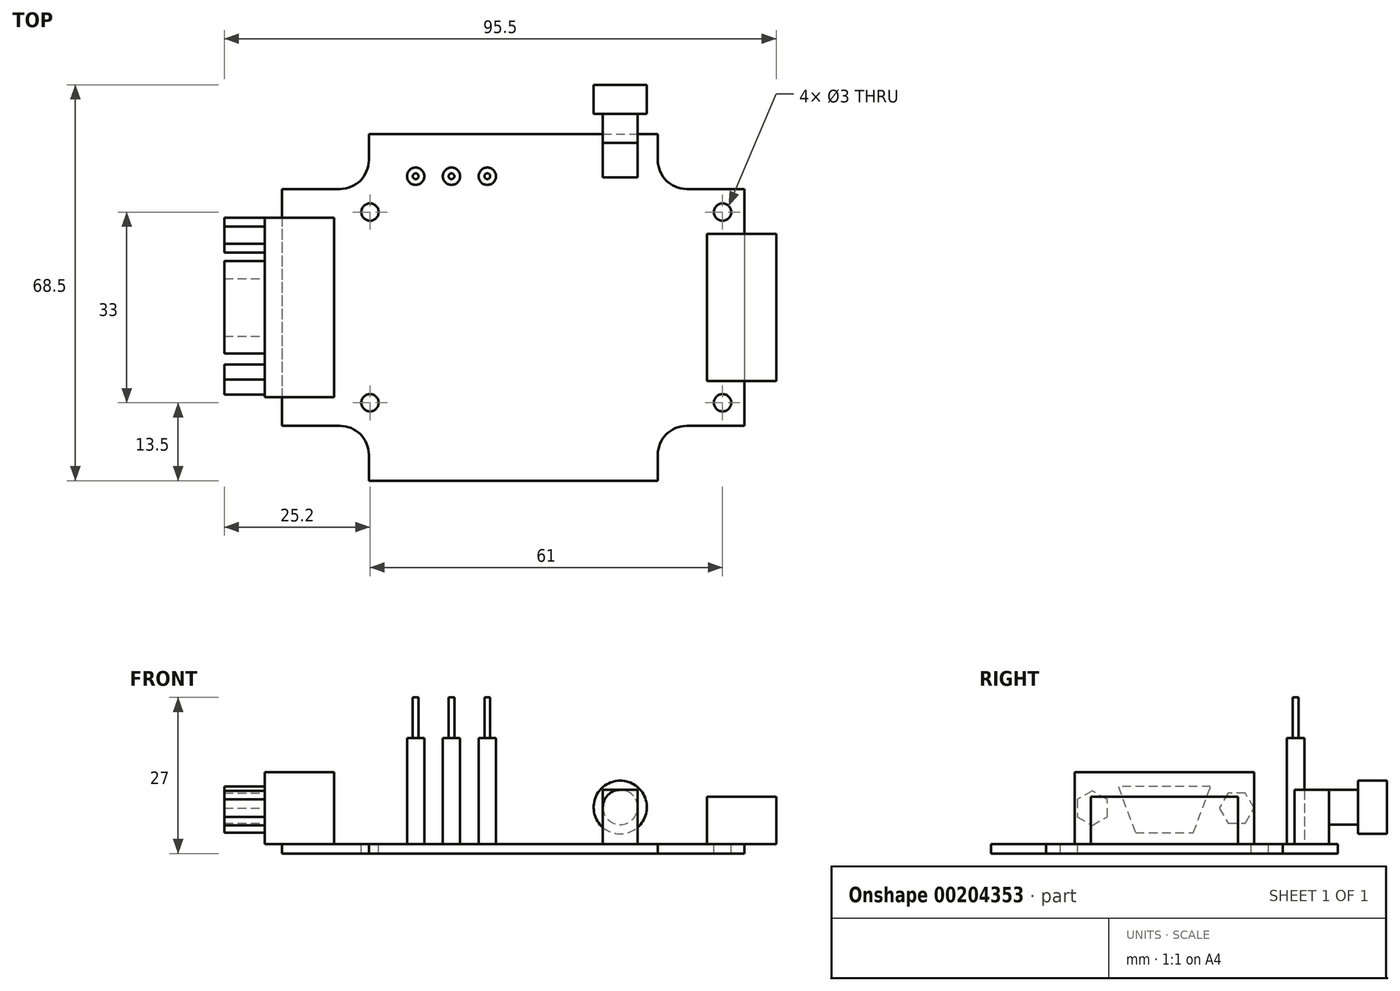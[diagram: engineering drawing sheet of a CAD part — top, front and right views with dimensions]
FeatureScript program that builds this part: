
annotation { "Feature Type Name" : "Feature", "Feature Type Description" : "" }
export const myFeature = defineFeature(function(context is Context, id is Id, definition is map)
    precondition{}
    {
        {
            var Q0;
            Q0=qCreatedBy(makeId("Top.planeOp"),FACE);
            var sketch = newSketch(context, id + "F0", { "sketchPlane" : qUnion([Q0])});
            skLineSegment(sketch, "E0.bottom", {"start": v(-40, 20.5) * mm, "end": v(40, 20.5) * mm});
            skLineSegment(sketch, "E0.top", {"start": v(-40, -20.5) * mm, "end": v(40, -20.5) * mm});
            skLineSegment(sketch, "E0.left", {"start": v(-40, 20.5) * mm, "end": v(-40, -20.5) * mm});
            skLineSegment(sketch, "E0.right", {"start": v(40, 20.5) * mm, "end": v(40, -20.5) * mm});
            skPoint(sketch, "E0.middle", {"position": v(0, 0) * mm});
            skLineSegment(sketch, "E1", {"start": v(0, 20.5) * mm, "end": v(-25, 20.5) * mm});
            skLineSegment(sketch, "E2", {"start": v(-25, 20.5) * mm, "end": v(-25, 30) * mm});
            skLineSegment(sketch, "E3", {"start": v(-25, 30) * mm, "end": v(25, 30) * mm});
            skLineSegment(sketch, "E4", {"start": v(25, 30) * mm, "end": v(25, 20.5) * mm});
            skLineSegment(sketch, "E5", {"start": v(25, 20.5) * mm, "end": v(0, 20.5) * mm});
            skLineSegment(sketch, "E6", {"start": v(0, -20.5) * mm, "end": v(-25, -20.5) * mm});
            skLineSegment(sketch, "E7", {"start": v(-25, -20.5) * mm, "end": v(-25, -30) * mm});
            skLineSegment(sketch, "E8", {"start": v(-25, -30) * mm, "end": v(25, -30) * mm});
            skLineSegment(sketch, "E9", {"start": v(25, -30) * mm, "end": v(25, -20.5) * mm});
            skLineSegment(sketch, "E10", {"start": v(25, -20.5) * mm, "end": v(0, -20.5) * mm});
            skSolve(sketch);
        }
        {
            var Q0;
            Q0=qSketchRegion(id+"F0",true);
            extrude(context, id + "F1", {"entities" : qUnion([Q0]), "depth" : 1.6 * mm});
        }
        {
            var Q0;
            Q0=makeQuery(id+"F1.opExtrude","CAP_FACE",FACE,{"disambiguationData":[OSD([sQuery(id+"F0.wireOp",EDGE,"E0.bottom"),sQuery(id+"F0.wireOp",EDGE,"E0.top"),sQuery(id+"F0.wireOp",EDGE,"E0.left"),sQuery(id+"F0.wireOp",EDGE,"E0.right")])],"isStart":false});
            var sketch = newSketch(context, id + "F2", { "sketchPlane" : qUnion([Q0])});
            skLineSegment(sketch, "E11", {"start": v(40, 0) * mm, "end": v(40, 12.75) * mm});
            skLineSegment(sketch, "E12", {"start": v(40, 12.75) * mm, "end": v(45.5, 12.75) * mm});
            skLineSegment(sketch, "E13", {"start": v(45.5, 12.75) * mm, "end": v(45.5, -12.75) * mm});
            skLineSegment(sketch, "E14", {"start": v(45.5, -12.75) * mm, "end": v(40, -12.75) * mm});
            skLineSegment(sketch, "E15", {"start": v(40, -12.75) * mm, "end": v(40, 0) * mm});
            skLineSegment(sketch, "E16", {"start": v(40, 12.75) * mm, "end": v(33.5, 12.75) * mm});
            skLineSegment(sketch, "E17", {"start": v(33.5, 12.75) * mm, "end": v(33.5, -12.75) * mm});
            skLineSegment(sketch, "E18", {"start": v(33.5, -12.75) * mm, "end": v(40, -12.75) * mm});
            skSolve(sketch);
        }
        {
            var Q0;
            Q0=qSketchRegion(id+"F2",true);
            extrude(context, id + "F3", {"entities" : qUnion([Q0]), "operationType" : NewBodyOperationType.ADD, "depth" : 8.24 * mm});
        }
        {
            var Q0;
            Q0=makeQuery(id+"F1.opExtrude","CAP_FACE",FACE,{"disambiguationData":[OSD([sQuery(id+"F0.wireOp",EDGE,"E0.bottom"),sQuery(id+"F0.wireOp",EDGE,"E0.top"),sQuery(id+"F0.wireOp",EDGE,"E0.left"),sQuery(id+"F0.wireOp",EDGE,"E0.right")])],"isStart":false});
            var sketch = newSketch(context, id + "F4", { "sketchPlane" : qUnion([Q0])});
            skLineSegment(sketch, "E19", {"start": v(-40, 0) * mm, "end": v(-40, 15.5) * mm});
            skLineSegment(sketch, "E20", {"start": v(-40, 15.5) * mm, "end": v(-43, 15.5) * mm});
            skLineSegment(sketch, "E21", {"start": v(-43, 15.5) * mm, "end": v(-43, -15.5) * mm});
            skLineSegment(sketch, "E22", {"start": v(-43, -15.5) * mm, "end": v(-40, -15.5) * mm});
            skLineSegment(sketch, "E23", {"start": v(-40, -15.5) * mm, "end": v(-40, 0) * mm});
            skLineSegment(sketch, "E24", {"start": v(-40, 15.5) * mm, "end": v(-31, 15.5) * mm});
            skLineSegment(sketch, "E25", {"start": v(-31, 15.5) * mm, "end": v(-31, -15.5) * mm});
            skLineSegment(sketch, "E26", {"start": v(-31, -15.5) * mm, "end": v(-40, -15.5) * mm});
            skSolve(sketch);
        }
        {
            var Q0;
            Q0=qSketchRegion(id+"F4",true);
            extrude(context, id + "F5", {"entities" : qUnion([Q0]), "operationType" : NewBodyOperationType.ADD, "depth" : 12.5 * mm});
        }
        {
            var Q0;
            Q0=makeQuery(id+"F5.opExtrude","SWEPT_FACE",FACE,{"disambiguationData":[OSD([sQuery(id+"F4.wireOp",EDGE,"E21")])]});
            var sketch = newSketch(context, id + "F6", { "sketchPlane" : qUnion([Q0])});
            skLineSegment(sketch, "E27", {"start": v(0, 1.6) * mm, "end": v(0, 3.6) * mm});
            skPoint(sketch, "E27.endSnap0", {"position": v(0, 1.6) * mm});
            skLineSegment(sketch, "E28", {"start": v(0, 3.6) * mm, "end": v(-5, 3.6) * mm});
            skLineSegment(sketch, "E29", {"start": v(-5, 3.6) * mm, "end": v(-8, 11.6) * mm});
            skLineSegment(sketch, "E30", {"start": v(-8, 11.6) * mm, "end": v(0, 11.6) * mm});
            skLineSegment(sketch, "E31", {"start": v(0, 11.6) * mm, "end": v(8, 11.6) * mm});
            skLineSegment(sketch, "E32", {"start": v(8, 11.6) * mm, "end": v(5, 3.6) * mm});
            skLineSegment(sketch, "E33", {"start": v(5, 3.6) * mm, "end": v(0, 3.6) * mm});
            skLineSegment(sketch, "E34", {"start": v(0, 11.6) * mm, "end": v(0, 3.6) * mm});
            skLineSegment(sketch, "E35", {"start": v(15.5, 1.6) * mm, "end": v(15.5, 7.85) * mm});
            skLineSegment(sketch, "E36", {"start": v(-15.5, 1.6) * mm, "end": v(-15.5, 7.85) * mm});
            skLineSegment(sketch, "E37", {"start": v(-15.5, 7.85) * mm, "end": v(-12.5, 7.85) * mm});
            skCircle(sketch, "E38.cCircle", {"center": v(-12.5, 7.85) * mm, "radius": 3 * mm, "construction": true});
            skLineSegment(sketch, "E38.0", {"start": v(-15.5, 7.85) * mm, "end": v(-14, 10.45) * mm});
            skLineSegment(sketch, "E38.1", {"start": v(-14, 10.45) * mm, "end": v(-11, 10.45) * mm});
            skLineSegment(sketch, "E38.2", {"start": v(-11, 10.45) * mm, "end": v(-9.5, 7.85) * mm});
            skLineSegment(sketch, "E38.3", {"start": v(-9.5, 7.85) * mm, "end": v(-11, 5.25) * mm});
            skLineSegment(sketch, "E38.4", {"start": v(-11, 5.25) * mm, "end": v(-14, 5.25) * mm});
            skLineSegment(sketch, "E38.5", {"start": v(-14, 5.25) * mm, "end": v(-15.5, 7.85) * mm});
            skLineSegment(sketch, "E39", {"start": v(15.5, 7.85) * mm, "end": v(12.5, 7.85) * mm});
            skCircle(sketch, "E40.cCircle", {"center": v(12.5, 7.85) * mm, "radius": 3 * mm, "construction": true});
            skLineSegment(sketch, "E40.0", {"start": v(12.5, 10.85) * mm, "end": v(15.1, 9.35) * mm});
            skLineSegment(sketch, "E40.1", {"start": v(15.1, 9.35) * mm, "end": v(15.1, 6.35) * mm});
            skLineSegment(sketch, "E40.2", {"start": v(15.1, 6.35) * mm, "end": v(12.5, 4.85) * mm});
            skLineSegment(sketch, "E40.3", {"start": v(12.5, 4.85) * mm, "end": v(9.9, 6.35) * mm});
            skLineSegment(sketch, "E40.4", {"start": v(9.9, 6.35) * mm, "end": v(9.9, 9.35) * mm});
            skLineSegment(sketch, "E40.5", {"start": v(9.9, 9.35) * mm, "end": v(12.5, 10.85) * mm});
            skSolve(sketch);
        }
        {
            var Q0;
            Q0=qSketchRegion(id+"F6",true);
            extrude(context, id + "F7", {"entities" : qUnion([Q0]), "operationType" : NewBodyOperationType.ADD, "depth" : 7 * mm});
        }
        {
            var Q0;
            Q0=makeQuery(id+"F1.opExtrude","CAP_FACE",FACE,{"disambiguationData":[OSD([sQuery(id+"F0.wireOp",EDGE,"E0.bottom"),sQuery(id+"F0.wireOp",EDGE,"E0.top"),sQuery(id+"F0.wireOp",EDGE,"E0.left"),sQuery(id+"F0.wireOp",EDGE,"E0.right")])],"isStart":false});
            var sketch = newSketch(context, id + "F8", { "sketchPlane" : qUnion([Q0])});
            skLineSegment(sketch, "E41", {"start": v(40, 20.5) * mm, "end": v(36.2, 20.5) * mm});
            skLineSegment(sketch, "E42", {"start": v(36.2, 20.5) * mm, "end": v(36.2, 16.5) * mm});
            skLineSegment(sketch, "E43", {"start": v(-40, 20.5) * mm, "end": v(-24.8, 20.5) * mm});
            skLineSegment(sketch, "E44", {"start": v(-40, -20.5) * mm, "end": v(-24.8, -20.5) * mm});
            skLineSegment(sketch, "E45", {"start": v(40, -20.5) * mm, "end": v(36.2, -20.5) * mm});
            skLineSegment(sketch, "E46", {"start": v(36.2, -20.5) * mm, "end": v(36.2, -16.5) * mm});
            skCircle(sketch, "E47", {"center": v(36.2, 16.5) * mm, "radius": 1.5 * mm});
            skCircle(sketch, "E48", {"center": v(36.2, -16.5) * mm, "radius": 1.5 * mm});
            skLineSegment(sketch, "E49", {"start": v(36.2, 16.5) * mm, "end": v(36.2, 0) * mm});
            skLineSegment(sketch, "E50", {"start": v(36.2, 0) * mm, "end": v(36.2, -16.5) * mm});
            skLineSegment(sketch, "E51", {"start": v(-24.8, 20.5) * mm, "end": v(-24.8, 16.5) * mm});
            skLineSegment(sketch, "E52", {"start": v(-24.8, -20.5) * mm, "end": v(-24.8, -16.5) * mm});
            skCircle(sketch, "E53", {"center": v(-24.8, 16.5) * mm, "radius": 1.5 * mm});
            skCircle(sketch, "E54", {"center": v(-24.8, -16.5) * mm, "radius": 1.5 * mm});
            skLineSegment(sketch, "E55", {"start": v(-24.8, -20.5) * mm, "end": v(36.2, -20.5) * mm});
            skSolve(sketch);
        }
        {
            var Q0;
            Q0=qSketchRegion(id+"F8",true);
            extrude(context, id + "F9", {"entities" : qUnion([Q0]), "operationType" : NewBodyOperationType.REMOVE, "oppositeDirection" : true, "depth" : 2 * mm});
        }
        {
            var Q0;
            Q0=makeQuery(id+"F1.opExtrude","CAP_FACE",FACE,{"disambiguationData":[OSD([sQuery(id+"F0.wireOp",EDGE,"E0.bottom"),sQuery(id+"F0.wireOp",EDGE,"E0.top"),sQuery(id+"F0.wireOp",EDGE,"E0.left"),sQuery(id+"F0.wireOp",EDGE,"E0.right")])],"isStart":false});
            var sketch = newSketch(context, id + "F10", { "sketchPlane" : qUnion([Q0])});
            skLineSegment(sketch, "E56", {"start": v(-4.5, 22.7) * mm, "end": v(-10.7, 22.7) * mm});
            skLineSegment(sketch, "E57", {"start": v(-40, -20.5) * mm, "end": v(-10.7, -20.5) * mm});
            skLineSegment(sketch, "E58", {"start": v(-10.7, -20.5) * mm, "end": v(-10.7, -14.4) * mm});
            skCircle(sketch, "E59", {"center": v(-10.7, 22.7) * mm, "radius": 1.5 * mm});
            skCircle(sketch, "E60", {"center": v(-4.5, 22.7) * mm, "radius": 1.5 * mm});
            skLineSegment(sketch, "E61", {"start": v(-10.7, 22.7) * mm, "end": v(-10.7, 0) * mm});
            skLineSegment(sketch, "E62", {"start": v(-10.7, 0) * mm, "end": v(-10.7, -14.4) * mm});
            skLineSegment(sketch, "E63", {"start": v(-10.7, 22.7) * mm, "end": v(-16.9, 22.7) * mm});
            skCircle(sketch, "E64", {"center": v(-16.9, 22.7) * mm, "radius": 1.5 * mm});
            skLineSegment(sketch, "E65", {"start": v(-40, 20.5) * mm, "end": v(-40, 30) * mm});
            skLineSegment(sketch, "E66", {"start": v(-40, 30) * mm, "end": v(-4.5, 30) * mm});
            skLineSegment(sketch, "E67", {"start": v(-4.5, 30) * mm, "end": v(-4.5, 22.7) * mm});
            skLineSegment(sketch, "E68", {"start": v(-4.5, 30) * mm, "end": v(0, 30) * mm});
            skSolve(sketch);
        }
        {
            var Q0;
            Q0=qSketchRegion(id+"F10",true);
            extrude(context, id + "F11", {"entities" : qUnion([Q0]), "operationType" : NewBodyOperationType.ADD, "depth" : 18.4 * mm});
        }
        {
            var Q0;
            Q0=makeQuery(id+"F11.opExtrude","CAP_FACE",FACE,{"disambiguationData":[OSD([sQuery(id+"F10.wireOp",EDGE,"E59")])],"isStart":false});
            var sketch = newSketch(context, id + "F12", { "sketchPlane" : qUnion([Q0])});
            skCircle(sketch, "E69", {"center": v(-10.7, 22.7) * mm, "radius": 0.5 * mm});
            skSolve(sketch);
        }
        {
            var Q0;
            Q0=qSketchRegion(id+"F12",true);
            extrude(context, id + "F13", {"entities" : qUnion([Q0]), "operationType" : NewBodyOperationType.ADD, "depth" : 7 * mm});
        }
        {
            var Q0;
            Q0=makeQuery(id+"F11.opExtrude","CAP_FACE",FACE,{"disambiguationData":[OSD([sQuery(id+"F10.wireOp",EDGE,"E60")])],"isStart":false});
            var sketch = newSketch(context, id + "F14", { "sketchPlane" : qUnion([Q0])});
            skCircle(sketch, "E70", {"center": v(-4.5, 22.7) * mm, "radius": 0.5 * mm});
            skSolve(sketch);
        }
        {
            var Q0;
            Q0=qSketchRegion(id+"F14",true);
            extrude(context, id + "F15", {"entities" : qUnion([Q0]), "operationType" : NewBodyOperationType.ADD, "depth" : 7 * mm});
        }
        {
            var Q0;
            Q0=makeQuery(id+"F1.opExtrude","CAP_FACE",FACE,{"disambiguationData":[OSD([sQuery(id+"F0.wireOp",EDGE,"E0.bottom"),sQuery(id+"F0.wireOp",EDGE,"E0.top"),sQuery(id+"F0.wireOp",EDGE,"E0.left"),sQuery(id+"F0.wireOp",EDGE,"E0.right")])],"isStart":false});
            var sketch = newSketch(context, id + "F16", { "sketchPlane" : qUnion([Q0])});
            skLineSegment(sketch, "E71", {"start": v(-57.5, 20.5) * mm, "end": v(-57.5, 30) * mm});
            skLineSegment(sketch, "E72", {"start": v(-57.5, 30) * mm, "end": v(-7.5, 30) * mm});
            skLineSegment(sketch, "E73", {"start": v(-7.5, 30) * mm, "end": v(-7.5, 20.5) * mm});
            skLineSegment(sketch, "E74", {"start": v(-7.5, 20.5) * mm, "end": v(-32.5, 20.5) * mm});
            skLineSegment(sketch, "E75", {"start": v(-32.5, 20.5) * mm, "end": v(-57.5, 20.5) * mm});
            skLineSegment(sketch, "E76", {"start": v(-32.5, -20.5) * mm, "end": v(-57.5, -20.5) * mm});
            skLineSegment(sketch, "E77", {"start": v(-57.5, -20.5) * mm, "end": v(-57.5, -31.8) * mm});
            skLineSegment(sketch, "E78", {"start": v(-57.5, -31.8) * mm, "end": v(-7.5, -31.8) * mm});
            skLineSegment(sketch, "E79", {"start": v(-7.5, -31.8) * mm, "end": v(-7.5, -20.5) * mm});
            skLineSegment(sketch, "E80", {"start": v(-7.5, -20.5) * mm, "end": v(-32.5, -20.5) * mm});
            skSolve(sketch);
        }
        {
            var Q0;
            Q0 = qSketchRegion(id + "F16", true);
            extrude(context, id + "F17", {"entities" : qUnion([Q0]), "oppositeDirection" : true, "depth" : 1.6 * mm});
        }
        {
            var Q0;
            Q0=makeQuery(id+"F17.opExtrude","SWEPT_BODY",BODY,{"disambiguationData":[OSD([sQuery(id+"F16.wireOp",EDGE,"E71"),sQuery(id+"F16.wireOp",EDGE,"E72"),sQuery(id+"F16.wireOp",EDGE,"E73"),sQuery(id+"F16.wireOp",EDGE,"E74"),sQuery(id+"F16.wireOp",EDGE,"E75")])]});
            deleteBodies(context, id + "F18", {"entities" : qUnion([Q0])});
        }
        {
            var Q0;
            Q0=makeQuery(id+"F17.opExtrude","SWEPT_BODY",BODY,{"disambiguationData":[OSD([sQuery(id+"F16.wireOp",EDGE,"E76"),sQuery(id+"F16.wireOp",EDGE,"E77"),sQuery(id+"F16.wireOp",EDGE,"E78"),sQuery(id+"F16.wireOp",EDGE,"E79"),sQuery(id+"F16.wireOp",EDGE,"E80")])]});
            deleteBodies(context, id + "F19", {"entities" : qUnion([Q0])});
        }
        {
            var Q0;
            Q0=makeQuery(id+"F1.opExtrude","SWEPT_EDGE",EDGE,{"disambiguationData":[OSD([sQuery(id+"F0.wireOp",EDGE,"E0.bottom"),sQuery(id+"F0.wireOp",EDGE,"E1"),sQuery(id+"F0.wireOp",EDGE,"E2")])]});
            var Q1;
            Q1=makeQuery(id+"F1.opExtrude","SWEPT_EDGE",EDGE,{"disambiguationData":[OSD([sQuery(id+"F0.wireOp",EDGE,"E0.bottom"),sQuery(id+"F0.wireOp",EDGE,"E4"),sQuery(id+"F0.wireOp",EDGE,"E5")])]});
            var Q2;
            Q2=makeQuery(id+"F1.opExtrude","SWEPT_EDGE",EDGE,{"disambiguationData":[OSD([sQuery(id+"F0.wireOp",EDGE,"E0.top"),sQuery(id+"F0.wireOp",EDGE,"E9"),sQuery(id+"F0.wireOp",EDGE,"E10")])]});
            var Q3;
            Q3=makeQuery(id+"F1.opExtrude","SWEPT_EDGE",EDGE,{"disambiguationData":[OSD([sQuery(id+"F0.wireOp",EDGE,"E0.top"),sQuery(id+"F0.wireOp",EDGE,"E6"),sQuery(id+"F0.wireOp",EDGE,"E7")])]});
            fillet(context, id + "F20", {"entities" : qUnion([Q0, Q1, Q2, Q3]), "radius" : 5 * mm, "tangentPropagation" : true, "allowEdgeOverflow" : false});
        }
        {
            var Q0;
            Q0=makeQuery(id+"F1.opExtrude","CAP_FACE",FACE,{"disambiguationData":[OSD([sQuery(id+"F0.wireOp",EDGE,"E0.bottom"),sQuery(id+"F0.wireOp",EDGE,"E0.top"),sQuery(id+"F0.wireOp",EDGE,"E0.left"),sQuery(id+"F0.wireOp",EDGE,"E0.right"),sQuery(id+"F0.wireOp",EDGE,"E2"),sQuery(id+"F0.wireOp",EDGE,"E3"),sQuery(id+"F0.wireOp",EDGE,"E4"),sQuery(id+"F0.wireOp",EDGE,"E7"),sQuery(id+"F0.wireOp",EDGE,"E8"),sQuery(id+"F0.wireOp",EDGE,"E9")])],"isStart":false});
            var sketch = newSketch(context, id + "F21", { "sketchPlane" : qUnion([Q0])});
            skLineSegment(sketch, "E81", {"start": v(40, 20.5) * mm, "end": v(40, 30) * mm});
            skLineSegment(sketch, "E82", {"start": v(40, 30) * mm, "end": v(18.5, 30) * mm});
            skLineSegment(sketch, "E83", {"start": v(18.5, 30) * mm, "end": v(18.5, 28.5) * mm});
            skLineSegment(sketch, "E84", {"start": v(18.5, 28.5) * mm, "end": v(15.5, 28.5) * mm});
            skLineSegment(sketch, "E85", {"start": v(15.5, 28.5) * mm, "end": v(15.5, 22.5) * mm});
            skLineSegment(sketch, "E86", {"start": v(15.5, 22.5) * mm, "end": v(21.5, 22.5) * mm});
            skLineSegment(sketch, "E87", {"start": v(21.5, 22.5) * mm, "end": v(21.5, 28.5) * mm});
            skLineSegment(sketch, "E88", {"start": v(21.5, 28.5) * mm, "end": v(18.5, 28.5) * mm});
            skLineSegment(sketch, "E89", {"start": v(0, 30) * mm, "end": v(18.5, 30) * mm});
            skSolve(sketch);
        }
        {
            var Q0;
            Q0 = qSketchRegion(id + "F21", true);
            extrude(context, id + "F22", {"entities" : qUnion([Q0]), "operationType" : NewBodyOperationType.ADD, "depth" : 9.4 * mm});
        }
        {
            var Q0;
            Q0=makeQuery(id+"F22.opExtrude","SWEPT_FACE",FACE,{"disambiguationData":[OSD([sQuery(id+"F21.wireOp",EDGE,"E84"),sQuery(id+"F21.wireOp",EDGE,"E88")])]});
            var sketch = newSketch(context, id + "F23", { "sketchPlane" : qUnion([Q0])});
            skLineSegment(sketch, "E90", {"start": v(-18.5, 11) * mm, "end": v(-18.5, 8) * mm});
            skCircle(sketch, "E91", {"center": v(-18.5, 8) * mm, "radius": 3 * mm});
            skSolve(sketch);
        }
        {
            var Q0;
            Q0 = qSketchRegion(id + "F23", true);
            extrude(context, id + "F24", {"entities" : qUnion([Q0]), "operationType" : NewBodyOperationType.ADD, "depth" : 7.5 * mm});
        }
        {
            var Q0;
            Q0=makeQuery(id+"F24.opExtrude","CAP_FACE",FACE,{"disambiguationData":[OSD([sQuery(id+"F23.wireOp",EDGE,"E91")])],"isStart":false});
            var sketch = newSketch(context, id + "F25", { "sketchPlane" : qUnion([Q0])});
            skCircle(sketch, "E92", {"center": v(-18.5, 8) * mm, "radius": 4.6 * mm});
            skSolve(sketch);
        }
        {
            var Q0;
            Q0 = qSketchRegion(id + "F25", true);
            extrude(context, id + "F26", {"entities" : qUnion([Q0]), "operationType" : NewBodyOperationType.ADD, "endBound" : BoundingType.SYMMETRIC, "oppositeDirection" : true, "depth" : 5 * mm});
        }
        {
            var Q0;
            Q0=makeQuery(id+"F11.opExtrude","CAP_FACE",FACE,{"disambiguationData":[OSD([sQuery(id+"F10.wireOp",EDGE,"E64")])],"isStart":false});
            var sketch = newSketch(context, id + "F27", { "sketchPlane" : qUnion([Q0])});
            skCircle(sketch, "E93", {"center": v(-16.9, 22.7) * mm, "radius": 0.5 * mm});
            skSolve(sketch);
        }
        {
            var Q0;
            Q0 = qSketchRegion(id + "F27", true);
            extrude(context, id + "F28", {"entities" : qUnion([Q0]), "operationType" : NewBodyOperationType.ADD, "depth" : 7 * mm});
        }
    });
